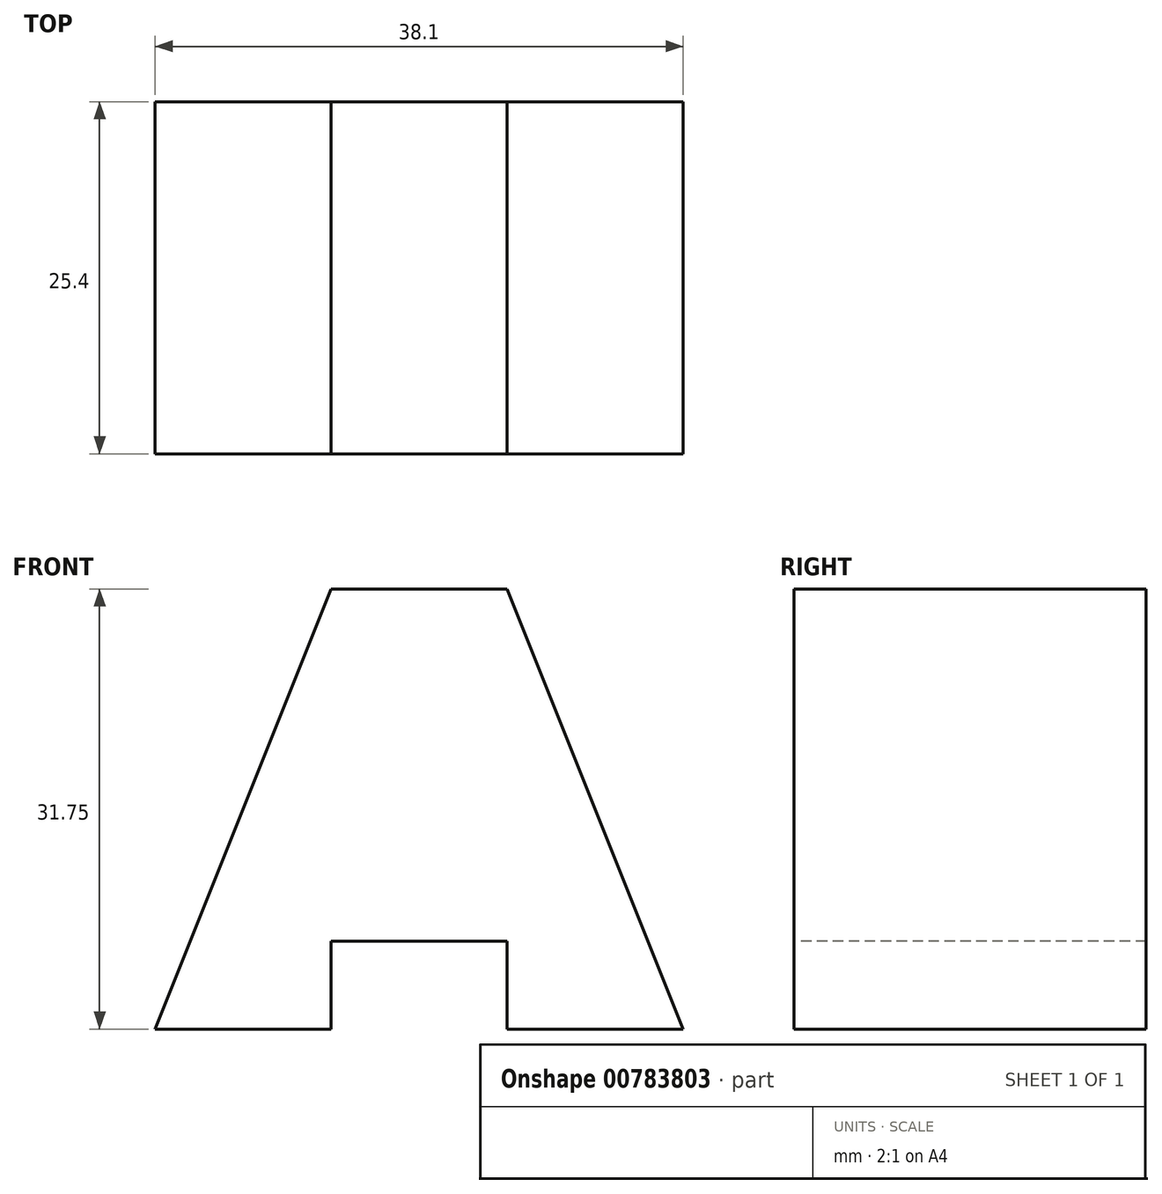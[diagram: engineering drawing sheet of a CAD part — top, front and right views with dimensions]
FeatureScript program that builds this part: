
annotation { "Feature Type Name" : "Feature", "Feature Type Description" : "" }
export const myFeature = defineFeature(function(context is Context, id is Id, definition is map)
    precondition{}
    {
        {
            var Q0;
            Q0=qCreatedBy(makeId("Front.planeOp"),FACE);
            var sketch = newSketch(context, id + "F0", { "sketchPlane" : qUnion([Q0])});
            skLineSegment(sketch, "E0", {"start": v(0, 0) * mm, "end": v(38.1, 0) * mm});
            skLineSegment(sketch, "E1", {"start": v(38.1, 0) * mm, "end": v(38.1, 31.75) * mm});
            skLineSegment(sketch, "E2", {"start": v(38.1, 31.75) * mm, "end": v(0, 31.75) * mm});
            skLineSegment(sketch, "E3", {"start": v(0, 31.75) * mm, "end": v(0, 0) * mm});
            skSolve(sketch);
        }
        {
            var Q0;
            Q0=makeQuery(id+"F0.imprint","IMPRINT",FACE,{"disambiguationData":[TD([[makeQuery(id+"F0.imprint","IMPRINT",EDGE,{"derivedFrom":sQuery(id+"F0.wireOp",EDGE,"E0")}),1.0]])]});
            extrude(context, id + "F1", {"entities" : qUnion([Q0]), "depth" : 25.4 * mm, "offsetDistance" : 25.4 * mm});
        }
        {
            var Q0;
            Q0=makeQuery(id+"F1.opExtrude","CAP_FACE",FACE,{"disambiguationData":[OSD([sQuery(id+"F0.wireOp",EDGE,"E0"),sQuery(id+"F0.wireOp",EDGE,"E1"),sQuery(id+"F0.wireOp",EDGE,"E2"),sQuery(id+"F0.wireOp",EDGE,"E3")])],"isStart":false});
            var sketch = newSketch(context, id + "F2", { "sketchPlane" : qUnion([Q0])});
            skLineSegment(sketch, "E4", {"start": v(0, 0) * mm, "end": v(12.7, 0) * mm});
            skLineSegment(sketch, "E5", {"start": v(12.7, 0) * mm, "end": v(12.7, 6.35) * mm});
            skLineSegment(sketch, "E6", {"start": v(12.7, 6.35) * mm, "end": v(25.4, 6.35) * mm});
            skLineSegment(sketch, "E7", {"start": v(25.4, 6.35) * mm, "end": v(25.4, 0) * mm});
            skLineSegment(sketch, "E8", {"start": v(25.4, 0) * mm, "end": v(38.1, 0) * mm});
            skSolve(sketch);
        }
        {
            var Q0;
            {var subQ0=sQuery(id+"F2.wireOp",EDGE,"E5");Q0=makeQuery(id+"F2.imprint","IMPRINT",FACE,{"disambiguationData":[TD([[makeQuery(id+"F2.imprint","IMPRINT",EDGE,{"derivedFrom":subQ0}),-1.0]])]});}
            extrude(context, id + "F3", {"entities" : qUnion([Q0]), "operationType" : NewBodyOperationType.REMOVE, "oppositeDirection" : true, "depth" : 25.4 * mm, "offsetDistance" : 25.4 * mm});
        }
        {
            var Q0;
            Q0=makeQuery(id+"F1.opExtrude","CAP_FACE",FACE,{"disambiguationData":[OSD([sQuery(id+"F0.wireOp",EDGE,"E0"),sQuery(id+"F0.wireOp",EDGE,"E1"),sQuery(id+"F0.wireOp",EDGE,"E2"),sQuery(id+"F0.wireOp",EDGE,"E3")])],"isStart":false});
            var sketch = newSketch(context, id + "F4", { "sketchPlane" : qUnion([Q0])});
            skLineSegment(sketch, "E9", {"start": v(38.1, 0) * mm, "end": v(25.4, 31.75) * mm});
            skLineSegment(sketch, "E10", {"start": v(12.7, 31.75) * mm, "end": v(25.4, 31.75) * mm});
            skLineSegment(sketch, "E11", {"start": v(0, 0) * mm, "end": v(12.7, 31.75) * mm});
            skSolve(sketch);
        }
        {
            var Q0;
            {var subQ0=sQuery(id+"F4.wireOp",EDGE,"E11");Q0=makeQuery(id+"F4.imprint","IMPRINT",FACE,{"disambiguationData":[TD([[makeQuery(id+"F4.imprint","IMPRINT",EDGE,{"derivedFrom":subQ0}),1.0]])]});}
            extrude(context, id + "F5", {"entities" : qUnion([Q0]), "operationType" : NewBodyOperationType.REMOVE, "oppositeDirection" : true, "depth" : 25.4 * mm, "offsetDistance" : 25.4 * mm});
        }
        {
            var Q0;
            Q0=makeQuery(id+"F1.opExtrude","CAP_FACE",FACE,{"disambiguationData":[OSD([sQuery(id+"F0.wireOp",EDGE,"E0"),sQuery(id+"F0.wireOp",EDGE,"E1"),sQuery(id+"F0.wireOp",EDGE,"E2"),sQuery(id+"F0.wireOp",EDGE,"E3")])],"isStart":false});
            var sketch = newSketch(context, id + "F6", { "sketchPlane" : qUnion([Q0])});
            skLineSegment(sketch, "E12", {"start": v(12.7, 31.75) * mm, "end": v(25.4, 31.75) * mm});
            skLineSegment(sketch, "E13", {"start": v(25.4, 31.75) * mm, "end": v(38.1, 0) * mm});
            skSolve(sketch);
        }
        {
            var Q0;
            {var subQ0=sQuery(id+"F6.wireOp",EDGE,"E13");Q0=makeQuery(id+"F6.imprint","IMPRINT",FACE,{"disambiguationData":[TD([[makeQuery(id+"F6.imprint","IMPRINT",EDGE,{"derivedFrom":subQ0}),1.0]])]});}
            extrude(context, id + "F7", {"entities" : qUnion([Q0]), "operationType" : NewBodyOperationType.REMOVE, "oppositeDirection" : true, "depth" : 25.4 * mm, "offsetDistance" : 25.4 * mm});
        }
    });
